# Revit family: Gira_5002003
name_source: partatom
category: Electrical Fixtures
revit_build: Autodesk Revit 2017 (Build: 20160225_1515(x64)
units: mm (PartAtom-declared; Revit-internal decimal feet)

## family parameters
Cut with Voids When Loaded = No
Host = Face
Maintain Annotation Orientation = No
Part Type = Normal
Room Calculation Point = No
Round Connector Dimension = Use Diameter
Shared = No

## types (1)
- KNX PB sens.4 Komfort 2-g TS4 white
    BIM = https://media.live.bim.site TS4 2fach.rfa
    BIMSITE_PRODUCT_ID = e985cbce9b3eb2b275569727d29a7a2392371b13
    Bus connection included = Yes
    Colour = White
    Cost = 0 $
    Default Elevation = 1219 mm
    GTIN = 4010337070856
    HAN = 5002003
    HeinzeBIM = https://www.heinze.de
    Manufacturer = Gira
    Number of buttons = 2
    Radio frequent bidirectional = No
    Transparent = No
    URL = https://www.gira.de
    White = White
    With IR sensor = No
    With anti-theft/dismantling protection = Yes
    With display = No
    With label area = No
    With room temperature controller = No

## geometry (parser evidence)
native form markers: Blend x2, Sweep x3
no freeform markers — native parametric forms only
